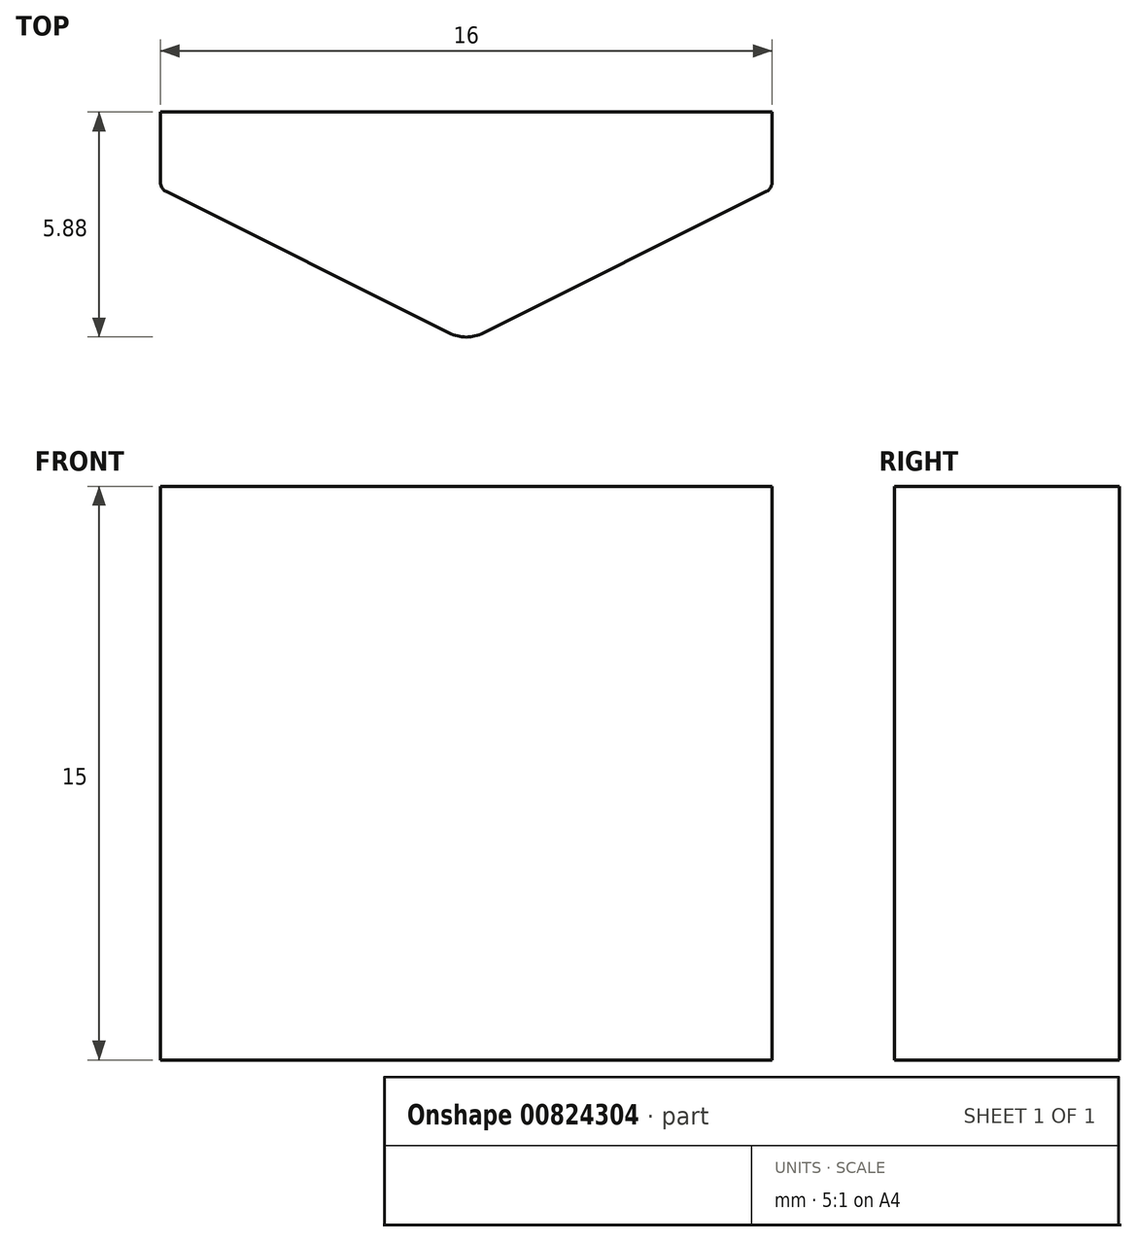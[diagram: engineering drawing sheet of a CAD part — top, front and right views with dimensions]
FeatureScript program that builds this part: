
annotation { "Feature Type Name" : "Feature", "Feature Type Description" : "" }
export const myFeature = defineFeature(function(context is Context, id is Id, definition is map)
    precondition{}
    {
        {
            var Q0;
            Q0=qCreatedBy(makeId("Top.planeOp"),FACE);
            var sketch = newSketch(context, id + "F0", { "sketchPlane" : qUnion([Q0])});
            skLineSegment(sketch, "E0", {"start": v(0, 6.67) * mm, "end": v(0, -16.48) * mm, "construction": true});
            skLineSegment(sketch, "E1", {"start": v(-19.74, 0) * mm, "end": v(16.3, 0) * mm, "construction": true});
            skLineSegment(sketch, "E2", {"start": v(-8, 0) * mm, "end": v(8, 0) * mm});
            skLineSegment(sketch, "E3", {"start": v(8, 0) * mm, "end": v(8, -1.81) * mm});
            skLineSegment(sketch, "E4", {"start": v(7.83, -2.08) * mm, "end": v(0.45, -5.78) * mm});
            skLineSegment(sketch, "E5", {"start": v(-0.45, -5.78) * mm, "end": v(-7.83, -2.08) * mm});
            skLineSegment(sketch, "E6", {"start": v(-8, -1.81) * mm, "end": v(-8, 0) * mm});
            skPoint(sketch, "E7.visualSharp", {"position": v(0, -6) * mm});
            skArc(sketch, "E7.filletArc", {"start": v(-0.45, -5.78) * mm, "mid": v(0, -5.88) * mm, "end": v(0.45, -5.78) * mm});
            skPoint(sketch, "E8.visualSharp", {"position": v(-8, -2) * mm});
            skArc(sketch, "E8.filletArc", {"start": v(-8, -1.81) * mm, "mid": v(-7.96, -1.97) * mm, "end": v(-7.83, -2.08) * mm});
            skPoint(sketch, "E9.visualSharp", {"position": v(8, -2) * mm});
            skArc(sketch, "E9.filletArc", {"start": v(7.83, -2.08) * mm, "mid": v(7.96, -1.97) * mm, "end": v(8, -1.81) * mm});
            skSolve(sketch);
        }
        {
            var Q0;
            Q0 = qSketchRegion(id + "F0", true);
            extrude(context, id + "F1", {"entities" : qUnion([Q0]), "oppositeDirection" : true, "depth" : 15 * mm, "offsetDistance" : 25 * mm});
        }
    });
